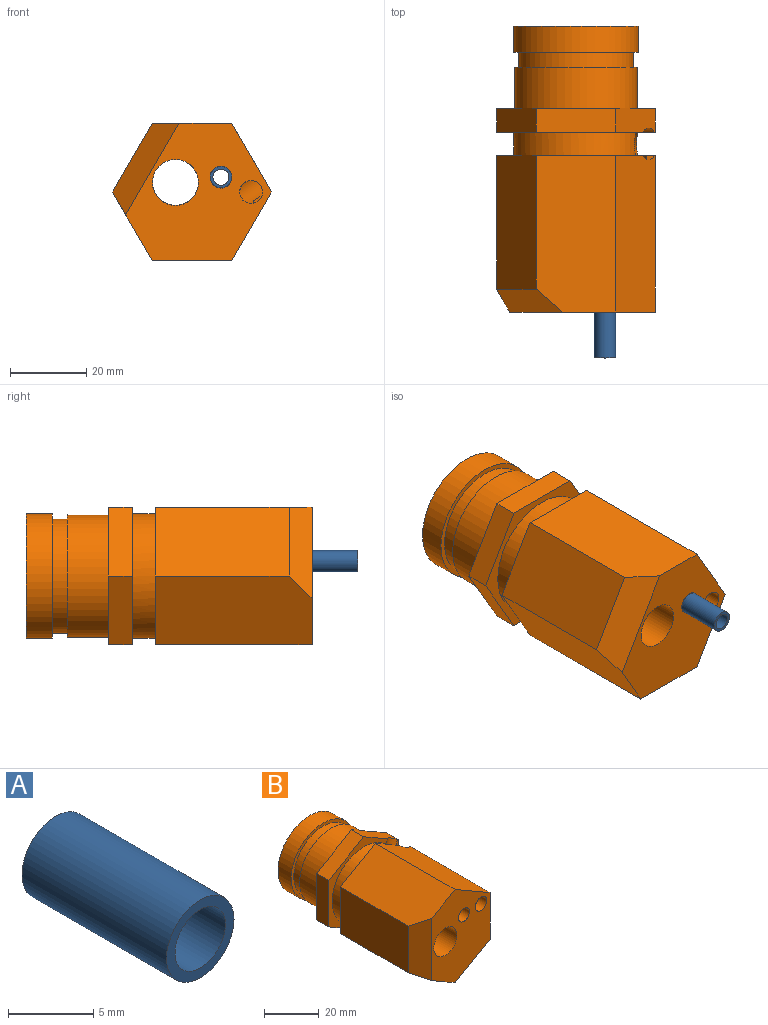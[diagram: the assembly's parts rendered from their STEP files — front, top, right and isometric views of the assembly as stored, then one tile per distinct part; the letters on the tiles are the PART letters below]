
ASSEMBLY  parts=2 mates=1
PART A: 4 faces, bbox 5.6x12x5.6 mm
  f0: cylinder r=2.1mm len=12mm, axis (0,-1,0), area 158.3mm2, adj f2,f3
  f1: cylinder r=2.8mm len=12mm, axis (0,-1,0), area 211.1mm2, adj f2,f3
  f2: plane 5.6x5.6mm, normal (0,1,0), area 10.8mm2, adj f0,f1
  f3: plane 5.6x5.6mm, normal (0,-1,0), area 10.8mm2, adj f0,f1
PART B: 34 faces, bbox 36.7x74.8x41.6 mm
  f0: plane 41.57x36mm, normal (0,1,0), area 265.5mm2, adj f1,f6,f7,f8,f9,f10,f11,f29
  f1: cylinder r=16.3mm len=32.6mm, axis (0,-1,0), area 560.3mm2, adj f0,f2,f29,f31
  f2: plane 41.57x36mm, normal (0,-1,0), area 267.1mm2, adj f1,f13,f14,f15,f16,f17,f18,f29
  f3: cylinder r=2.85mm len=25.61mm, axis (0,1,0), area 448.6mm2, adj f27,f29
  f4: cylinder r=2.85mm len=26mm, axis (0,1,0), area 457.1mm2, adj f5,f27,f29,f30
  f5: plane 5.38x4.17mm, normal (0,1,0), area 12.8mm2, adj f4,f30
  f6: plane 41x20.78mm, normal (1,0,0), area 852.2mm2, adj f0,f7,f11,f12
  f7: plane 41.01x18.01mm, normal (0.5,0,0.87), area 846.8mm2, adj f0,f6,f8,f12,f29
  f8: plane 41x18mm, normal (-0.5,0,0.87), area 831.4mm2, adj f0,f7,f9,f12,f32
  f9: plane 35x20.78mm, normal (-1,0,0), area 727.5mm2, adj f0,f8,f10,f32
  f10: plane 41x18mm, normal (-0.5,0,-0.87), area 831.4mm2, adj f0,f9,f11,f12,f32
  f11: plane 41x18mm, normal (0.5,0,-0.87), area 852.2mm2, adj f0,f6,f10,f12
  f12: plane 41.57x30mm, normal (0,-1,0), area 810mm2, adj f6,f7,f8,f10,f11,f28,f31,f32
  f13: plane 20.78x6.25mm, normal (-1,0,0), area 129.9mm2, adj f2,f14,f18,f19
  f14: plane 18x10.39mm, normal (-0.5,0,0.87), area 129.9mm2, adj f2,f13,f15,f19
  f15: plane 18.01x10.4mm, normal (0.5,0,0.87), area 124.5mm2, adj f2,f14,f16,f19,f29
  f16: plane 20.78x6.25mm, normal (1,0,0), area 129.9mm2, adj f2,f15,f17,f19
  f17: plane 18x10.39mm, normal (0.5,0,-0.87), area 129.9mm2, adj f2,f16,f18,f19
  f18: plane 18x10.39mm, normal (-0.5,0,-0.87), area 129.9mm2, adj f2,f13,f17,f19
  f19: plane 41.57x36mm, normal (0,1,0), area 318.1mm2, adj f13,f14,f15,f16,f17,f18,f20
  f20: cylinder r=16mm len=32mm, axis (0,-1,0), area 1080.7mm2, adj f19,f21
  f21: plane 32x32mm, normal (0,1,0), area 97.4mm2, adj f20,f22
  f22: cylinder r=15mm len=30mm, axis (0,-1,0), area 377mm2, adj f21,f25
  f23: cylinder r=16.35mm len=32.7mm, axis (0,-1,0), area 698.6mm2, adj f24,f25
  f24: plane 32.7x32.7mm, normal (0,1,0), area 254.5mm2, adj f23,f26
  f25: plane 32.7x32.7mm, normal (0,-1,0), area 133mm2, adj f22,f23
  f26: cylinder r=13.65mm len=27.3mm, axis (0,1,0), area 171.5mm2, adj f24,f27
  f27: plane 27.3x27.3mm, normal (0,1,0), area 395.7mm2, adj f3,f4,f26,f28,f33
  f28: cylinder r=6mm len=72.8mm, axis (0,1,0), area 2744.5mm2, adj f12,f27
  f29: cylinder r=4.28mm len=23.22mm, axis (-0.46,0,-0.89), area 450mm2, adj f0,f1,f2,f3,f4,f7,f15,f30
  f30: plane 7.58x7.46mm, normal (0.46,0,0.89), area 51mm2, adj f4,f5,f29
  f31: cylinder r=3mm len=41.62mm, axis (0,-1,0), area 760mm2, adj f0,f1,f12,f29
  f32: plane 27.71x6mm, normal (-0.71,-0.71,0), area 205.8mm2, adj f8,f9,f10,f12
  f33: cylinder r=2.85mm len=72.8mm, axis (0,1,0), area 1295.5mm2, adj f12,f27,f29
PLACE A rot(axis=(0.97,0,-0.26),180deg) t=(7.58,-20.5,21.88)mm
PLACE B rot(axis=(0,1,0),30deg) t=(0,-20.5,18)mm
MATE planar A.f0 <-> B.f33  axis (0,1,0) through (7.58,-20.5,21.88)mm
